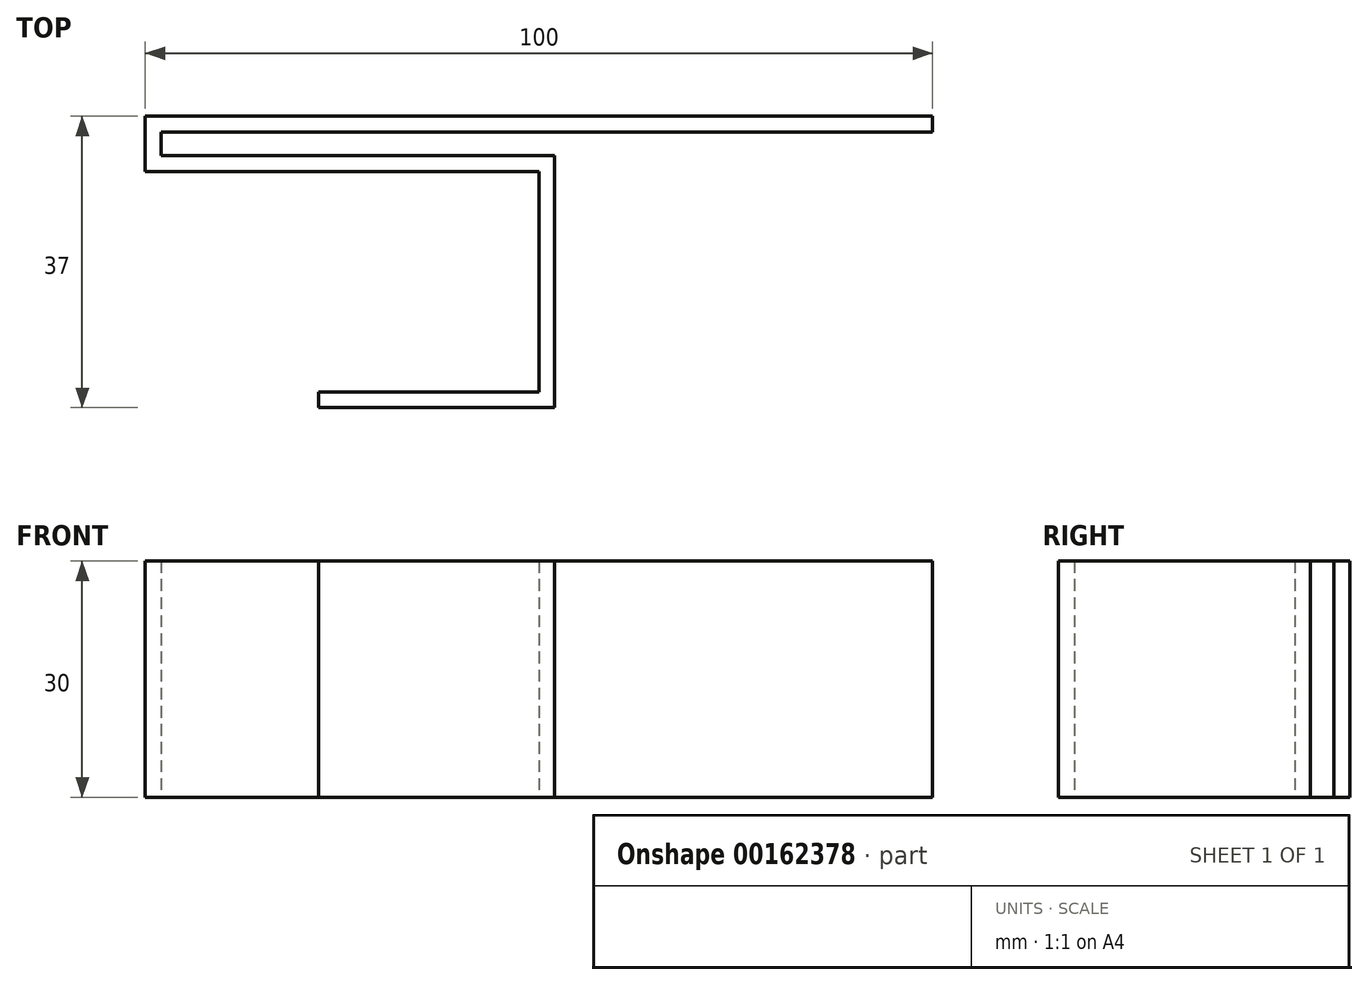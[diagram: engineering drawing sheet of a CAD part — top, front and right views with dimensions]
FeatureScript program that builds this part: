
annotation { "Feature Type Name" : "Feature", "Feature Type Description" : "" }
export const myFeature = defineFeature(function(context is Context, id is Id, definition is map)
    precondition{}
    {
        {
            var Q0;
            Q0=qCreatedBy(makeId("Top.planeOp"),FACE);
            var sketch = newSketch(context, id + "F0", { "sketchPlane" : qUnion([Q0])});
            skLineSegment(sketch, "E0", {"start": v(49.79, 13.04) * mm, "end": v(49.79, 15.04) * mm});
            skLineSegment(sketch, "E1", {"start": v(49.79, 15.04) * mm, "end": v(-50.21, 15.04) * mm});
            skLineSegment(sketch, "E2", {"start": v(-50.21, 15.04) * mm, "end": v(-50.21, 8.04) * mm});
            skLineSegment(sketch, "E3", {"start": v(-50.21, 8.04) * mm, "end": v(-0.21, 8.04) * mm});
            skLineSegment(sketch, "E4", {"start": v(-0.21, 8.04) * mm, "end": v(-0.21, -19.96) * mm});
            skLineSegment(sketch, "E5", {"start": v(-0.21, -19.96) * mm, "end": v(-28.21, -19.96) * mm});
            skLineSegment(sketch, "E6", {"start": v(-28.21, -19.96) * mm, "end": v(-28.21, -21.96) * mm});
            skLineSegment(sketch, "E7", {"start": v(-28.21, -21.96) * mm, "end": v(1.79, -21.96) * mm});
            skLineSegment(sketch, "E8", {"start": v(1.79, -21.96) * mm, "end": v(1.79, 10.04) * mm});
            skLineSegment(sketch, "E9", {"start": v(1.79, 10.04) * mm, "end": v(-48.21, 10.04) * mm});
            skLineSegment(sketch, "E10", {"start": v(-48.21, 10.04) * mm, "end": v(-48.21, 13.04) * mm});
            skLineSegment(sketch, "E11", {"start": v(-48.21, 13.04) * mm, "end": v(49.79, 13.04) * mm});
            skSolve(sketch);
        }
        {
            var Q0;
            Q0 = qSketchRegion(id + "F0", true);
            extrude(context, id + "F1", {"entities" : qUnion([Q0]), "depth" : 30 * mm});
        }
    });
